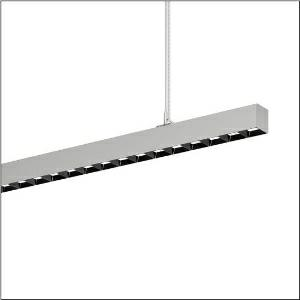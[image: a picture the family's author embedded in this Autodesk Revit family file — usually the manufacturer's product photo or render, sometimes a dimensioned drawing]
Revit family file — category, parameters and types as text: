
# Revit family: silica_r__21_51mx32dc3dsb_c9e6
name_source: partatom
category: Lighting Fixtures
units: mm (PartAtom-declared; Revit-internal decimal feet)

## family parameters
Cut with Voids When Loaded = No
Host = Face
Light Source = No
Part Type = Normal
Room Calculation Point = No
Round Connector Dimension = Use Diameter
Shared = No

## types (1)
- --- (1 x LED, 18220 lm, 113 W, 3000K)
    Apparent Load = 113 VA
    CIE Flux Codes = 86 99 100 59 100
    Color Rendering = 80
    Color Temperature = 3000K
    Default Elevation = 1800 mm
    Description = Silica® 21, office luminaire, primary light control with darklight reflector, of PMMA, black, CAT 2 (L<= 3000cd/m²), light emission: direct/indirect distribution, primary light characteristic: symmetric, installation type: suspended mounting, LED, rated luminous flux: 18.220lm, luminous efficacy: 161lm/W, light colour: 830, colour temperature: 3000K, with terminal, 3+2-pole, max. 2.5mm², mains connection: 220..240V, AC, 50/60Hz, rated input power: 113W, luminaire housing, of aluminium, metallic grey (RAL 9006), length: 3.004mm, width: 53mm, height: 53mm, protection rating (complete): IP20, insulation class (complete): insulation class I (protective earthing), certification: CE, permissible operating ambient temperature: 0..+35°C, standard: EN 50419, packaging unit: 1 piece
    Height = 53 mm
    Lamp = 1 x LED
    Lamp Light Flux = 18220 lm
    Lamp Power = 113 W
    Lamp count = 1
    Length = 3004 mm
    Luminous efficacy = 161 lm/W
    Manufacturer = Siteco
    ModVariant = No
    Model = 51MX32DC3DSB
    Mounting Place = Ceiling
    Mounting Type = Pendant
    Number of Poles = 1
    OnlyDefault = Yes
    Power Factor = 1
    Product Name = Silica® 21
    Product group = office luminaire | ceiling pendant
    ProductGroupID = 905
    Protection Class = Protection class I
    Protection Degree = IP 20
    RLX_Detail_Level = 1
    RlxData = <blob elided: 64993 chars, md5=e47f4402>
    Socket = socket
    Standby Power = 0 W
    System Light Flux = 18220 lm
    System Power = 113 W
    Type Comments = factory setting: luminous flux: 100 % | dim-lin: 254 | 391 mA
    Type Image = l_1251731.jpg
    URL = http://relux.com
    VarID = @adj_031127
    Voltage = 0 V
    Weight = 0.00 kg
    Width = 53 mm

## geometry (parser evidence)
native form markers: Blend x4, Sweep x11
no freeform markers — native parametric forms only
